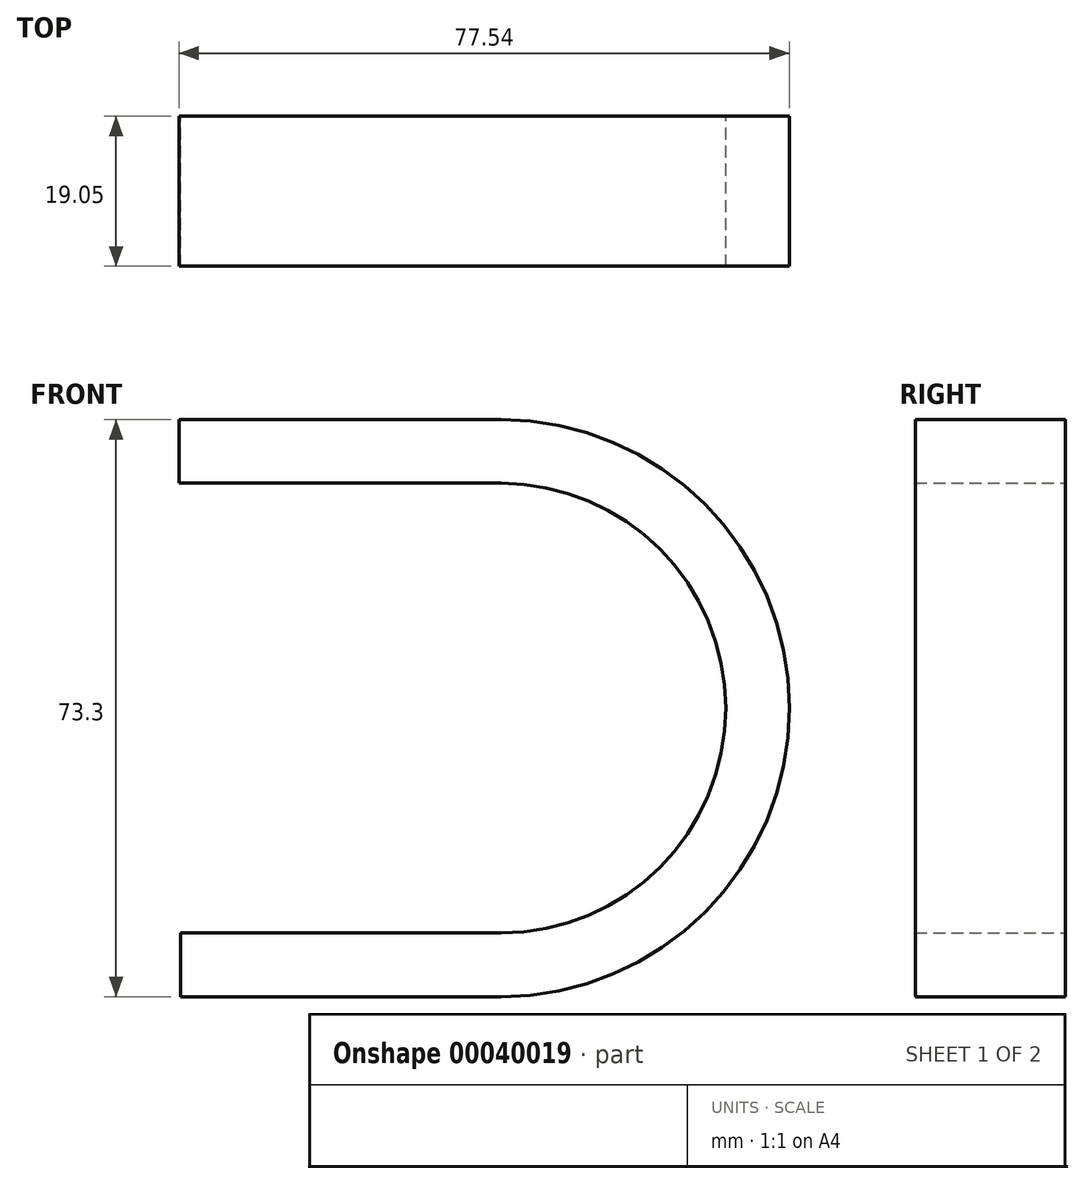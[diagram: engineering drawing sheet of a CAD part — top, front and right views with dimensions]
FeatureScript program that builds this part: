
annotation { "Feature Type Name" : "Feature", "Feature Type Description" : "" }
export const myFeature = defineFeature(function(context is Context, id is Id, definition is map)
    precondition{}
    {
        {
            var Q0;
            Q0=qCreatedBy(makeId("Front.planeOp"),FACE);
            var sketch = newSketch(context, id + "F0", { "sketchPlane" : qUnion([Q0])});
            skArc(sketch, "E0", {"start": v(0, -36.65) * mm, "mid": v(36.65, 0) * mm, "end": v(0, 36.65) * mm});
            skArc(sketch, "E1", {"start": v(0, -28.58) * mm, "mid": v(28.58, 0) * mm, "end": v(0, 28.58) * mm});
            skLineSegment(sketch, "E2", {"start": v(0, 36.65) * mm, "end": v(-40.89, 36.65) * mm});
            skLineSegment(sketch, "E3", {"start": v(0, -36.65) * mm, "end": v(-40.65, -36.65) * mm});
            skLineSegment(sketch, "E4", {"start": v(0, 28.58) * mm, "end": v(-40.89, 28.58) * mm});
            skLineSegment(sketch, "E5", {"start": v(0, -28.58) * mm, "end": v(-40.65, -28.58) * mm});
            skLineSegment(sketch, "E6", {"start": v(-40.89, 36.65) * mm, "end": v(-40.89, 28.58) * mm});
            skLineSegment(sketch, "E7", {"start": v(-40.65, -28.58) * mm, "end": v(-40.65, -36.65) * mm});
            skSolve(sketch);
        }
        {
            var Q0;
            Q0 = qSketchRegion(id + "F0", true);
            extrude(context, id + "F1", {"entities" : qUnion([Q0]), "depth" : 19.05 * mm});
        }
    });
